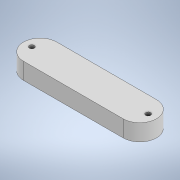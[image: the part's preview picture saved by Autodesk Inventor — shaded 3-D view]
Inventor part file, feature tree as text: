
AUTODESK INVENTOR PART (.ipt)
format: ipt  version: 2022 (Build 260153000, 153)  size: 110,080 bytes
history: native  units: mm
features: extrude x1, sketch x1
ambient origin geometry x8: Origin, YZ Plane, XZ Plane, XY Plane, X Axis, Y Axis, Z Axis, Center Point
bodies: Solid1 (feature_tree)
feature tree (2):
  extrude  "Extrusion1"  Depth=20.0mm
  sketch  "Sketch1"  dims[d0=80.0mm d1=20.0mm d3=35.0mm d4=0.0mm d5=35.0mm d6=180.0deg d7=3.0mm d8=3.0mm d9=10.0mm d10=0.0mm d11=10.0mm]
